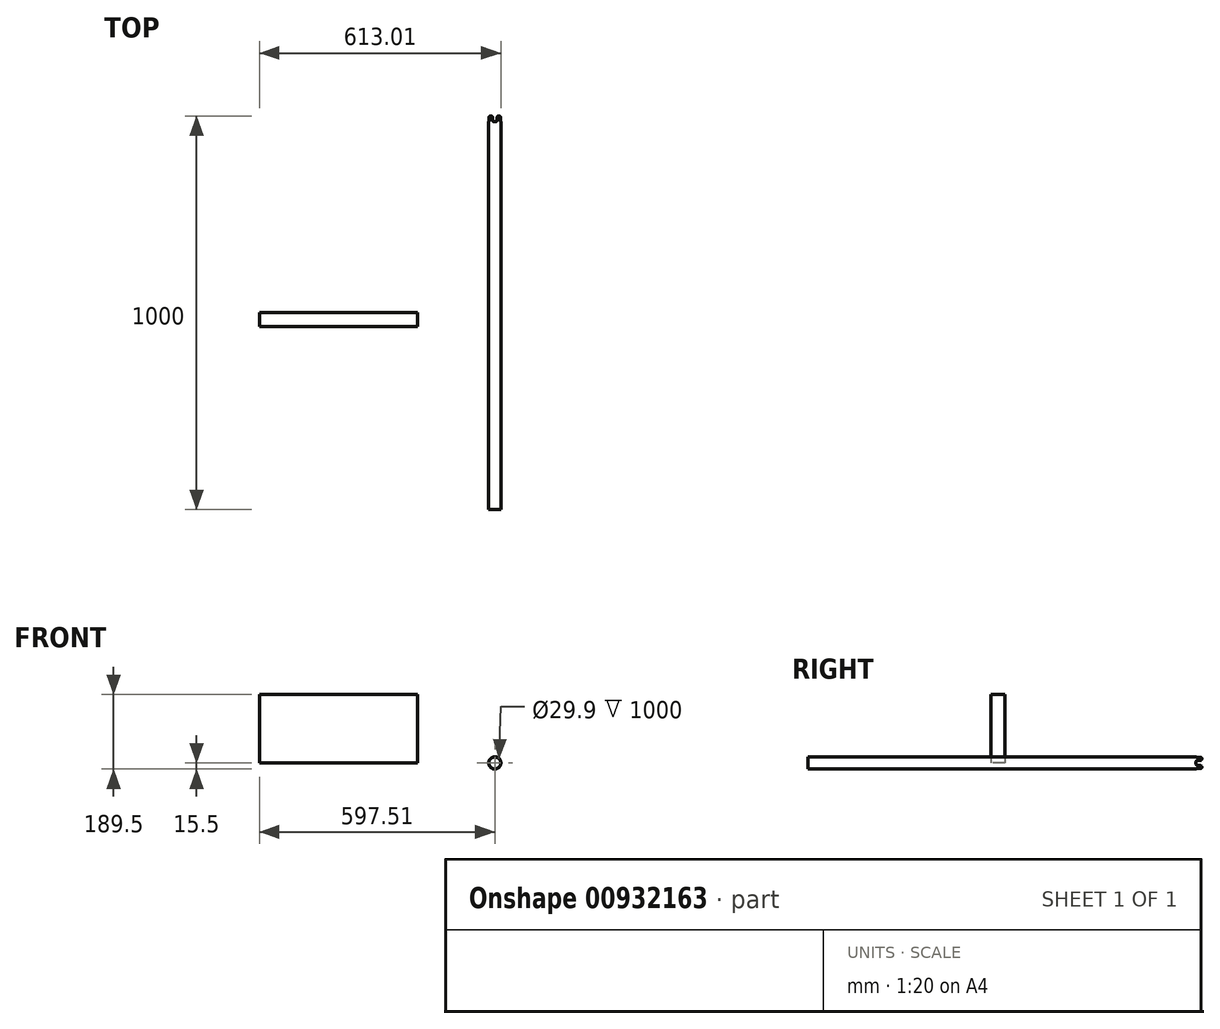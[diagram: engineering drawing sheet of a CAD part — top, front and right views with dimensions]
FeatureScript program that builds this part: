
annotation { "Feature Type Name" : "Feature", "Feature Type Description" : "" }
export const myFeature = defineFeature(function(context is Context, id is Id, definition is map)
    precondition{}
    {
        {
            var Q0;
            Q0=qCreatedBy(makeId("Front.planeOp"),FACE);
            var sketch = newSketch(context, id + "F0", { "sketchPlane" : qUnion([Q0])});
            skCircle(sketch, "E0", {"center": v(0, 0) * mm, "radius": 14.95 * mm});
            skCircle(sketch, "E1", {"center": v(0, 0) * mm, "radius": 15.5 * mm});
            skSolve(sketch);
        }
        {
            var Q0;
            Q0=makeQuery(id+"F0.imprint","IMPRINT",FACE,{"disambiguationData":[TD([[makeQuery(id+"F0.imprint","IMPRINT",EDGE,{"derivedFrom":sQuery(id+"F0.wireOp",EDGE,"E0")}),-1.0]])]});
            extrude(context, id + "F1", {"entities" : qUnion([Q0]), "depth" : 1000 * mm, "offsetDistance" : 25.4 * mm});
        }
        {
            var Q0;
            Q0=qCreatedBy(makeId("Top.planeOp"),FACE);
            var sketch = newSketch(context, id + "F2", { "sketchPlane" : qUnion([Q0])});
            skLineSegment(sketch, "E2.bottom", {"start": v(-2, -15) * mm, "end": v(2, -15) * mm});
            skLineSegment(sketch, "E2.top", {"start": v(-6, 15) * mm, "end": v(6, 15) * mm});
            skLineSegment(sketch, "E2.left", {"start": v(-6, -11) * mm, "end": v(-6, -4) * mm});
            skLineSegment(sketch, "E2.right", {"start": v(6, -11) * mm, "end": v(6, -4) * mm});
            skPoint(sketch, "E2.middle", {"position": v(0, 0) * mm});
            skPoint(sketch, "E3.visualSharp", {"position": v(-6, -15) * mm});
            skArc(sketch, "E3.filletArc", {"start": v(-6, -11) * mm, "mid": v(-4.83, -13.83) * mm, "end": v(-2, -15) * mm});
            skPoint(sketch, "E4.visualSharp", {"position": v(6, -15) * mm});
            skArc(sketch, "E4.filletArc", {"start": v(2, -15) * mm, "mid": v(4.83, -13.83) * mm, "end": v(6, -11) * mm});
            skLineSegment(sketch, "E5", {"start": v(-18.79, 0) * mm, "end": v(-6, 15) * mm});
            skLineSegment(sketch, "E6", {"start": v(20.75, 0) * mm, "end": v(6, 15) * mm});
            skLineSegment(sketch, "E7", {"start": v(-18.79, 0) * mm, "end": v(-10, 0) * mm});
            skLineSegment(sketch, "E8", {"start": v(10, 0) * mm, "end": v(20.75, 0) * mm});
            skPoint(sketch, "E9.visualSharp", {"position": v(-6, 0) * mm});
            skArc(sketch, "E9.filletArc", {"start": v(-6, -4) * mm, "mid": v(-7.17, -1.17) * mm, "end": v(-10, 0) * mm});
            skPoint(sketch, "E10.visualSharp", {"position": v(6, 0) * mm});
            skArc(sketch, "E10.filletArc", {"start": v(10, 0) * mm, "mid": v(7.17, -1.17) * mm, "end": v(6, -4) * mm});
            skSolve(sketch);
        }
        {
            var Q0;
            Q0=makeQuery(id+"F2.imprint","IMPRINT",FACE,{"disambiguationData":[TD([[makeQuery(id+"F2.imprint","IMPRINT",EDGE,{"derivedFrom":sQuery(id+"F2.wireOp",EDGE,"E2.top")}),-1.0]])]});
            extrude(context, id + "F3", {"entities" : qUnion([Q0]), "operationType" : NewBodyOperationType.REMOVE, "endBound" : BoundingType.SYMMETRIC, "depth" : 40 * mm, "offsetDistance" : 25 * mm});
        }
        {
            var Q0;
            Q0=qCreatedBy(makeId("Right.planeOp"),FACE);
            var sketch = newSketch(context, id + "F4", { "sketchPlane" : qUnion([Q0])});
            skLineSegment(sketch, "E11.bottom", {"start": v(-11, -6) * mm, "end": v(-4, -6) * mm});
            skLineSegment(sketch, "E11.top", {"start": v(-11, 6) * mm, "end": v(-4, 6) * mm});
            skLineSegment(sketch, "E11.left", {"start": v(-15, -2) * mm, "end": v(-15, 2) * mm});
            skPoint(sketch, "E11.middle", {"position": v(0, 0) * mm});
            skPoint(sketch, "E12.visualSharp", {"position": v(-15, 6) * mm});
            skArc(sketch, "E12.filletArc", {"start": v(-11, 6) * mm, "mid": v(-13.83, 4.83) * mm, "end": v(-15, 2) * mm});
            skPoint(sketch, "E13.visualSharp", {"position": v(-15, -6) * mm});
            skArc(sketch, "E13.filletArc", {"start": v(-15, -2) * mm, "mid": v(-13.83, -4.83) * mm, "end": v(-11, -6) * mm});
            skLineSegment(sketch, "E14.bottom", {"start": v(0, -16.35) * mm, "end": v(30, -16.35) * mm});
            skLineSegment(sketch, "E14.top", {"start": v(0, 16.35) * mm, "end": v(30, 16.35) * mm});
            skLineSegment(sketch, "E14.left", {"start": v(0, -16.35) * mm, "end": v(0, -10) * mm});
            skLineSegment(sketch, "E14.right", {"start": v(30, -16.35) * mm, "end": v(30, 16.35) * mm});
            skPoint(sketch, "E14.middle", {"position": v(15, 0) * mm});
            skPoint(sketch, "E15.orphan", {"position": v(15, 6) * mm});
            skPoint(sketch, "E11.right.start.orphan", {"position": v(15, -6) * mm});
            skLineSegment(sketch, "E16.trimOffspring", {"start": v(0, 10) * mm, "end": v(0, 16.35) * mm});
            skPoint(sketch, "E17.visualSharp", {"position": v(0, 6) * mm});
            skArc(sketch, "E17.filletArc", {"start": v(-4, 6) * mm, "mid": v(-1.17, 7.17) * mm, "end": v(0, 10) * mm});
            skPoint(sketch, "E18.visualSharp", {"position": v(0, -6) * mm});
            skArc(sketch, "E18.filletArc", {"start": v(0, -10) * mm, "mid": v(-1.17, -7.17) * mm, "end": v(-4, -6) * mm});
            skSolve(sketch);
        }
        {
            var Q0;
            Q0=makeQuery(id+"F4.imprint","IMPRINT",FACE,{"disambiguationData":[TD([[makeQuery(id+"F4.imprint","IMPRINT",EDGE,{"derivedFrom":sQuery(id+"F4.wireOp",EDGE,"E11.bottom")}),1.0]])]});
            extrude(context, id + "F5", {"entities" : qUnion([Q0]), "operationType" : NewBodyOperationType.REMOVE, "endBound" : BoundingType.SYMMETRIC, "depth" : 40 * mm, "offsetDistance" : 25 * mm});
        }
        {
            var Q0;
            Q0=qCreatedBy(makeId("Top.planeOp"),FACE);
            var sketch = newSketch(context, id + "F6", { "sketchPlane" : qUnion([Q0])});
            skLineSegment(sketch, "E19", {"start": v(0, 0) * mm, "end": v(0, -500) * mm});
            skLineSegment(sketch, "E20", {"start": v(0, -500) * mm, "end": v(-597.51, -500) * mm});
            skPoint(sketch, "E21.middle", {"position": v(-597.51, -500) * mm});
            skPoint(sketch, "E21.top.start.orphan", {"position": v(-302.25, -449.06) * mm});
            skPoint(sketch, "E21.right.end.orphan", {"position": v(-892.77, -449.06) * mm});
            skPoint(sketch, "E21.right.start.orphan", {"position": v(-892.77, -550.94) * mm});
            skPoint(sketch, "E21.left.start.orphan", {"position": v(-302.25, -550.94) * mm});
            skLineSegment(sketch, "E22.bottom", {"start": v(-597.51, -500) * mm, "end": v(-196.94, -500) * mm});
            skLineSegment(sketch, "E22.top", {"start": v(-597.51, -535.22) * mm, "end": v(-196.94, -535.22) * mm});
            skLineSegment(sketch, "E22.left", {"start": v(-597.51, -500) * mm, "end": v(-597.51, -535.22) * mm});
            skLineSegment(sketch, "E22.right", {"start": v(-196.94, -500) * mm, "end": v(-196.94, -535.22) * mm});
            skSolve(sketch);
        }
        {
            var Q0;
            Q0=makeQuery(id+"F6.imprint","IMPRINT",FACE,{"disambiguationData":[TD([[makeQuery(id+"F6.imprint","IMPRINT",EDGE,{"derivedFrom":sQuery(id+"F6.wireOp",EDGE,"E22.top")}),1.0]])]});
            extrude(context, id + "F7", {"entities" : qUnion([Q0]), "depth" : 174 * mm, "offsetDistance" : 25 * mm});
        }
    });
